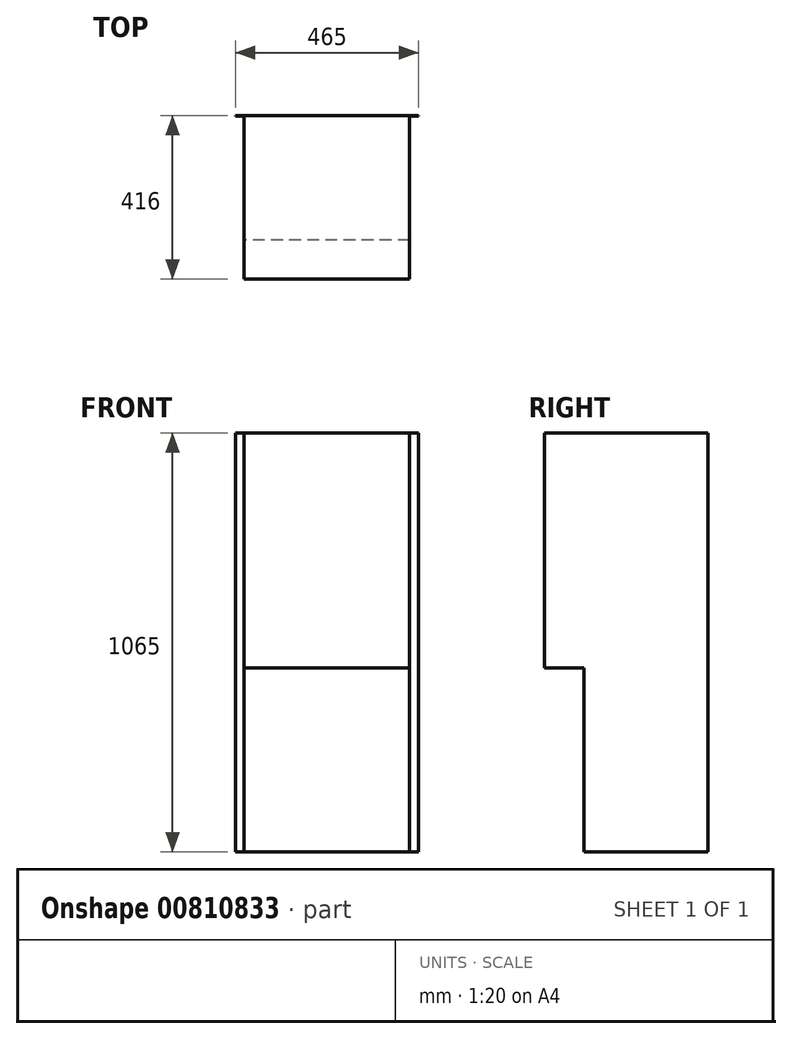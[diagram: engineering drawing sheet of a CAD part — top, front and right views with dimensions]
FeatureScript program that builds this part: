
annotation { "Feature Type Name" : "Feature", "Feature Type Description" : "" }
export const myFeature = defineFeature(function(context is Context, id is Id, definition is map)
    precondition{}
    {
        {
            var Q0;
            Q0=qCreatedBy(makeId("Front.planeOp"),FACE);
            var sketch = newSketch(context, id + "F0", { "sketchPlane" : qUnion([Q0])});
            skLineSegment(sketch, "E0.bottom", {"start": v(-232.5, 532.5) * mm, "end": v(232.5, 532.5) * mm});
            skLineSegment(sketch, "E0.top", {"start": v(-232.5, -532.5) * mm, "end": v(232.5, -532.5) * mm});
            skLineSegment(sketch, "E0.left", {"start": v(-232.5, 532.5) * mm, "end": v(-232.5, -532.5) * mm});
            skLineSegment(sketch, "E0.right", {"start": v(232.5, 532.5) * mm, "end": v(232.5, -532.5) * mm});
            skPoint(sketch, "E0.middle", {"position": v(0, 0) * mm});
            skSolve(sketch);
        }
        {
            var Q0;
            Q0=makeQuery(id+"F0.imprint","IMPRINT",FACE,{"disambiguationData":[TD([[makeQuery(id+"F0.imprint","IMPRINT",EDGE,{"derivedFrom":sQuery(id+"F0.wireOp",EDGE,"E0.bottom")}),-1.0]])]});
            extrude(context, id + "F1", {"entities" : qUnion([Q0]), "depth" : 1 * mm, "offsetDistance" : 25 * mm});
        }
        {
            var Q0;
            Q0=makeQuery(id+"F1.opExtrude","CAP_FACE",FACE,{"disambiguationData":[OSD([sQuery(id+"F0.wireOp",EDGE,"E0.bottom"),sQuery(id+"F0.wireOp",EDGE,"E0.top"),sQuery(id+"F0.wireOp",EDGE,"E0.left"),sQuery(id+"F0.wireOp",EDGE,"E0.right")])],"isStart":false});
            var sketch = newSketch(context, id + "F2", { "sketchPlane" : qUnion([Q0])});
            skLineSegment(sketch, "E1.bottom", {"start": v(-210, 532.5) * mm, "end": v(210, 532.5) * mm});
            skLineSegment(sketch, "E1.top", {"start": v(-210, -532.5) * mm, "end": v(210, -532.5) * mm});
            skLineSegment(sketch, "E1.left", {"start": v(-210, 532.5) * mm, "end": v(-210, -532.5) * mm});
            skLineSegment(sketch, "E1.right", {"start": v(210, 532.5) * mm, "end": v(210, -532.5) * mm});
            skPoint(sketch, "E1.middle", {"position": v(0, 0) * mm});
            skSolve(sketch);
        }
        {
            var Q0;
            Q0 = qSketchRegion(id + "F2", true);
            extrude(context, id + "F3", {"entities" : qUnion([Q0]), "operationType" : NewBodyOperationType.ADD, "depth" : 315 * mm, "offsetDistance" : 25 * mm});
        }
        {
            var Q0;
            Q0=makeQuery(id+"F3.opExtrude","CAP_FACE",FACE,{"disambiguationData":[OSD([sQuery(id+"F2.wireOp",EDGE,"E1.bottom"),sQuery(id+"F2.wireOp",EDGE,"E1.top"),sQuery(id+"F2.wireOp",EDGE,"E1.left"),sQuery(id+"F2.wireOp",EDGE,"E1.right")])],"isStart":false});
            var sketch = newSketch(context, id + "F4", { "sketchPlane" : qUnion([Q0])});
            skLineSegment(sketch, "E2.bottom", {"start": v(210, 532.5) * mm, "end": v(-210, 532.5) * mm});
            skLineSegment(sketch, "E2.top", {"start": v(210, -65.5) * mm, "end": v(-210, -65.5) * mm});
            skLineSegment(sketch, "E2.left", {"start": v(210, 532.5) * mm, "end": v(210, -65.5) * mm});
            skLineSegment(sketch, "E2.right", {"start": v(-210, 532.5) * mm, "end": v(-210, -65.5) * mm});
            skSolve(sketch);
        }
        {
            var Q0;
            Q0 = qSketchRegion(id + "F4", true);
            extrude(context, id + "F5", {"entities" : qUnion([Q0]), "operationType" : NewBodyOperationType.ADD, "depth" : 100 * mm, "offsetDistance" : 25 * mm});
        }
    });
